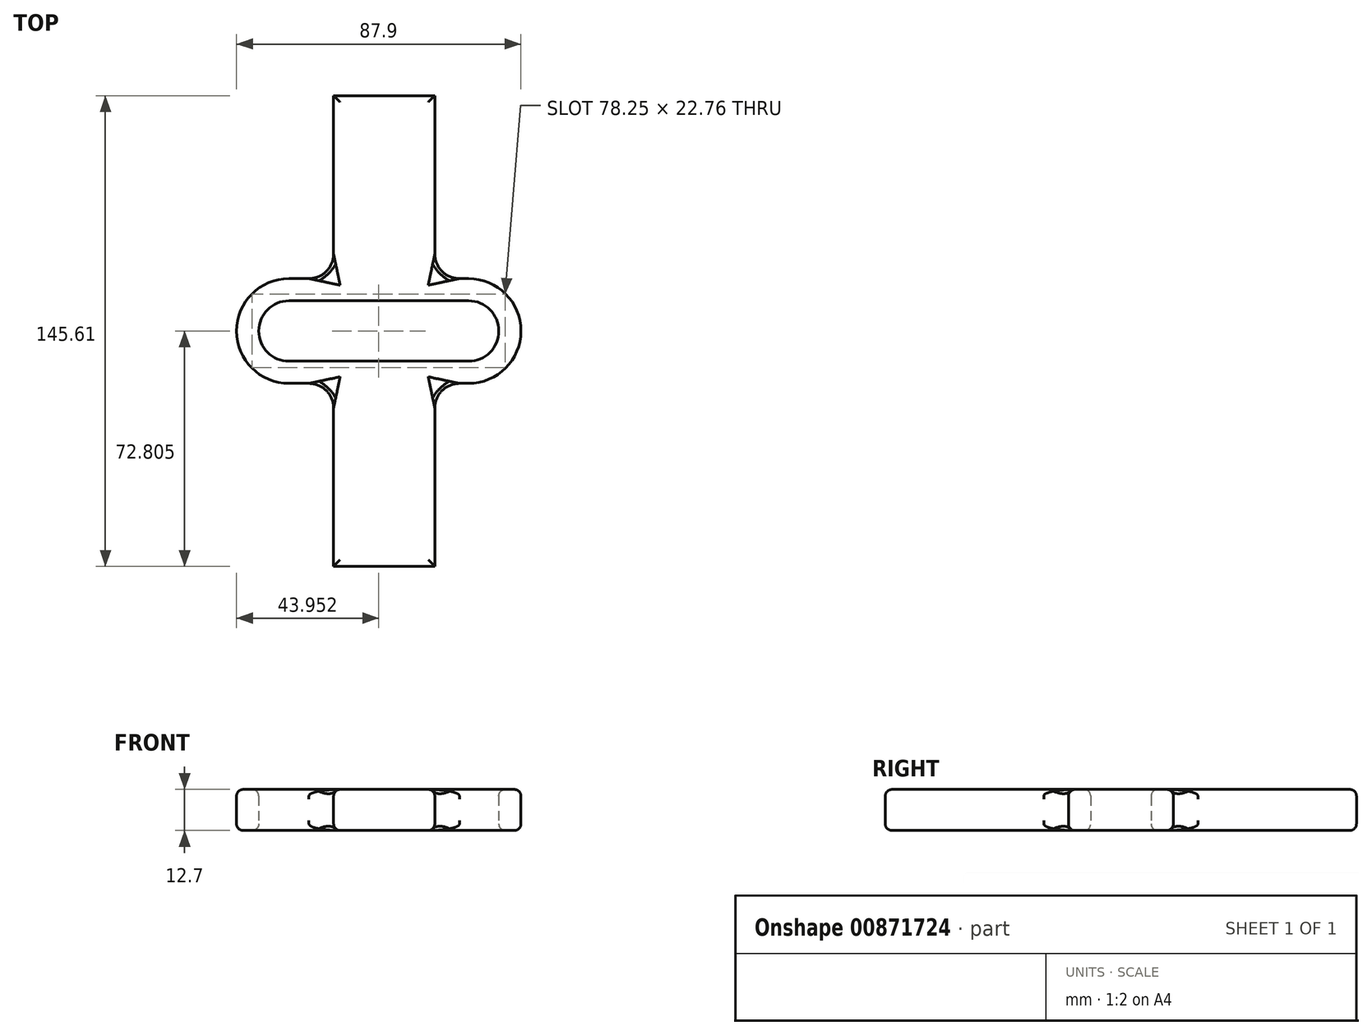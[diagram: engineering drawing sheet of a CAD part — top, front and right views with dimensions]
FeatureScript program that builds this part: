
annotation { "Feature Type Name" : "Feature", "Feature Type Description" : "" }
export const myFeature = defineFeature(function(context is Context, id is Id, definition is map)
    precondition{}
    {
        {
            var Q0;
            Q0=qCreatedBy(makeId("Top.planeOp"),FACE);
            var sketch = newSketch(context, id + "F0", { "sketchPlane" : qUnion([Q0])});
            skLineSegment(sketch, "E0", {"start": v(-24.83, -12.42) * mm, "end": v(30.66, -12.42) * mm});
            skArc(sketch, "E1", {"start": v(30.66, -12.42) * mm, "mid": v(40, -3.07) * mm, "end": v(30.66, 6.28) * mm});
            skLineSegment(sketch, "E2", {"start": v(30.66, 6.28) * mm, "end": v(-24.83, 6.28) * mm});
            skArc(sketch, "E3", {"start": v(-24.83, 6.28) * mm, "mid": v(-34.18, -3.07) * mm, "end": v(-24.83, -12.42) * mm});
            skLineSegment(sketch, "E4.0", {"start": v(30.66, 13.14) * mm, "end": v(20.23, 13.14) * mm});
            skArc(sketch, "E4.1", {"start": v(30.66, -19.27) * mm, "mid": v(46.86, -3.07) * mm, "end": v(30.66, 13.14) * mm});
            skLineSegment(sketch, "E4.2", {"start": v(-24.83, -19.27) * mm, "end": v(-11.04, -19.27) * mm});
            skArc(sketch, "E4.3", {"start": v(-24.83, 13.14) * mm, "mid": v(-41.04, -3.07) * mm, "end": v(-24.83, -19.27) * mm});
            skLineSegment(sketch, "E5.left", {"start": v(-11.04, 13.14) * mm, "end": v(-11.04, 13.14) * mm});
            skLineSegment(sketch, "E5.right", {"start": v(20.23, 13.14) * mm, "end": v(20.23, 13.14) * mm});
            skLineSegment(sketch, "E6.top", {"start": v(-11.04, 69.74) * mm, "end": v(20.23, 69.74) * mm});
            skLineSegment(sketch, "E6.left", {"start": v(-11.04, 13.14) * mm, "end": v(-11.04, 69.74) * mm});
            skLineSegment(sketch, "E6.right", {"start": v(20.23, 13.14) * mm, "end": v(20.23, 69.74) * mm});
            skLineSegment(sketch, "E7.MirrorCS", {"start": v(-11.04, -19.27) * mm, "end": v(-11.04, -75.87) * mm});
            skLineSegment(sketch, "E8.MirrorCS", {"start": v(-11.04, -75.87) * mm, "end": v(20.23, -75.87) * mm});
            skLineSegment(sketch, "E9.MirrorCS", {"start": v(20.23, -19.27) * mm, "end": v(20.23, -75.87) * mm});
            skLineSegment(sketch, "E10.trimOffspring", {"start": v(-11.04, 13.14) * mm, "end": v(-24.83, 13.14) * mm});
            skLineSegment(sketch, "E11.trimOffspring", {"start": v(20.23, -19.27) * mm, "end": v(30.66, -19.27) * mm});
            skSolve(sketch);
        }
        {
            var Q0;
            Q0 = qSketchRegion(id + "F0", true);
            extrude(context, id + "F1", {"entities" : qUnion([Q0]), "depth" : 12.7 * mm, "offsetDistance" : 25.4 * mm});
        }
        {
            var Q0;
            Q0=makeQuery(id+"F1.opExtrude","CAP_FACE",FACE,{"disambiguationData":[OSD([sQuery(id+"F0.wireOp",EDGE,"E0"),sQuery(id+"F0.wireOp",EDGE,"E1"),sQuery(id+"F0.wireOp",EDGE,"E2"),sQuery(id+"F0.wireOp",EDGE,"E3"),sQuery(id+"F0.wireOp",EDGE,"E4.0"),sQuery(id+"F0.wireOp",EDGE,"E4.1"),sQuery(id+"F0.wireOp",EDGE,"E4.2"),sQuery(id+"F0.wireOp",EDGE,"E4.3"),sQuery(id+"F0.wireOp",EDGE,"E6.top"),sQuery(id+"F0.wireOp",EDGE,"E6.left"),sQuery(id+"F0.wireOp",EDGE,"E6.right"),sQuery(id+"F0.wireOp",EDGE,"E7.MirrorCS"),sQuery(id+"F0.wireOp",EDGE,"E8.MirrorCS"),sQuery(id+"F0.wireOp",EDGE,"E9.MirrorCS"),sQuery(id+"F0.wireOp",EDGE,"E10.trimOffspring"),sQuery(id+"F0.wireOp",EDGE,"E11.trimOffspring")])],"isStart":false});
            fillet(context, id + "F2", {"entities" : qUnion([Q0]), "radius" : 2.03 * mm, "tangentPropagation" : true, "allowEdgeOverflow" : false});
        }
        {
            var Q0;
            Q0=makeQuery(id+"F1.opExtrude","CAP_FACE",FACE,{"disambiguationData":[OSD([sQuery(id+"F0.wireOp",EDGE,"E0"),sQuery(id+"F0.wireOp",EDGE,"E1"),sQuery(id+"F0.wireOp",EDGE,"E2"),sQuery(id+"F0.wireOp",EDGE,"E3"),sQuery(id+"F0.wireOp",EDGE,"E4.0"),sQuery(id+"F0.wireOp",EDGE,"E4.1"),sQuery(id+"F0.wireOp",EDGE,"E4.2"),sQuery(id+"F0.wireOp",EDGE,"E4.3"),sQuery(id+"F0.wireOp",EDGE,"E6.top"),sQuery(id+"F0.wireOp",EDGE,"E6.left"),sQuery(id+"F0.wireOp",EDGE,"E6.right"),sQuery(id+"F0.wireOp",EDGE,"E7.MirrorCS"),sQuery(id+"F0.wireOp",EDGE,"E8.MirrorCS"),sQuery(id+"F0.wireOp",EDGE,"E9.MirrorCS"),sQuery(id+"F0.wireOp",EDGE,"E10.trimOffspring"),sQuery(id+"F0.wireOp",EDGE,"E11.trimOffspring")])],"isStart":true});
            fillet(context, id + "F3", {"entities" : qUnion([Q0]), "radius" : 2.03 * mm, "tangentPropagation" : true, "allowEdgeOverflow" : false});
        }
        {
            var Q0;
            Q0=makeQuery(id+"F1.opExtrude","SWEPT_EDGE",EDGE,{"disambiguationData":[OSD([sQuery(id+"F0.wireOp",EDGE,"E6.left"),sQuery(id+"F0.wireOp",EDGE,"E10.trimOffspring")])]});
            var Q1;
            Q1=makeQuery(id+"F1.opExtrude","SWEPT_EDGE",EDGE,{"disambiguationData":[OSD([sQuery(id+"F0.wireOp",EDGE,"E4.0"),sQuery(id+"F0.wireOp",EDGE,"E6.right")])]});
            var Q2;
            Q2=makeQuery(id+"F1.opExtrude","SWEPT_EDGE",EDGE,{"disambiguationData":[OSD([sQuery(id+"F0.wireOp",EDGE,"E9.MirrorCS"),sQuery(id+"F0.wireOp",EDGE,"E11.trimOffspring")])]});
            var Q3;
            Q3=makeQuery(id+"F1.opExtrude","SWEPT_EDGE",EDGE,{"disambiguationData":[OSD([sQuery(id+"F0.wireOp",EDGE,"E4.2"),sQuery(id+"F0.wireOp",EDGE,"E7.MirrorCS")])]});
            fillet(context, id + "F4", {"entities" : qUnion([Q0, Q1, Q2, Q3]), "radius" : 7.62 * mm, "tangentPropagation" : true, "allowEdgeOverflow" : false});
        }
    });
